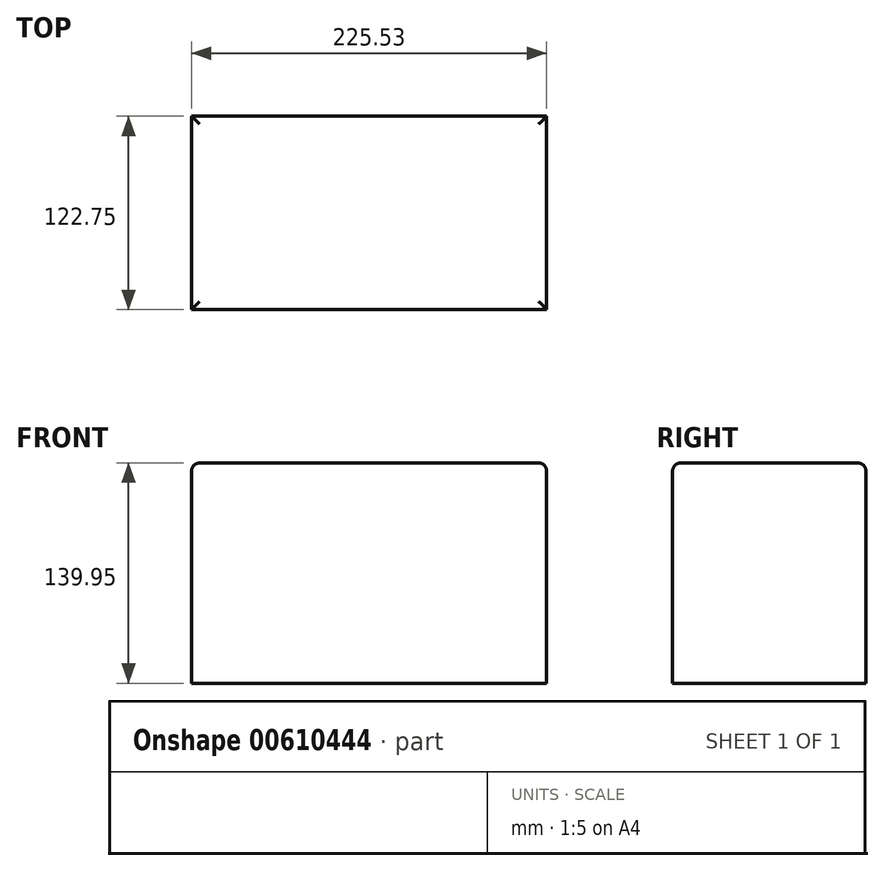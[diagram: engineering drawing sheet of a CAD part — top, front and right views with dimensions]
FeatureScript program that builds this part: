
annotation { "Feature Type Name" : "Feature", "Feature Type Description" : "" }
export const myFeature = defineFeature(function(context is Context, id is Id, definition is map)
    precondition{}
    {
        {
            var Q0;
            Q0=qCreatedBy(makeId("Top.planeOp"),FACE);
            var sketch = newSketch(context, id + "F0", { "sketchPlane" : qUnion([Q0])});
            skLineSegment(sketch, "E0.bottom", {"start": v(-109.76, -69.81) * mm, "end": v(115.77, -69.81) * mm});
            skLineSegment(sketch, "E0.top", {"start": v(-109.76, 52.94) * mm, "end": v(115.77, 52.94) * mm});
            skLineSegment(sketch, "E0.left", {"start": v(-109.76, -69.81) * mm, "end": v(-109.76, 52.94) * mm});
            skLineSegment(sketch, "E0.right", {"start": v(115.77, -69.81) * mm, "end": v(115.77, 52.94) * mm});
            skLineSegment(sketch, "E1.0", {"start": v(-103.4, -69.81) * mm, "end": v(-103.4, 52.94) * mm});
            skSolve(sketch);
        }
        {
            var Q0;
            Q0 = qSketchRegion(id + "F0", true);
            extrude(context, id + "F1", {"entities" : qUnion([Q0]), "depth" : 139.95 * mm, "offsetDistance" : 25.4 * mm});
        }
        {
            var Q0;
            Q0=makeQuery(id+"F1.opExtrude","CAP_EDGE",EDGE,{"disambiguationData":[OSD([sQuery(id+"F0.wireOp",EDGE,"E0.bottom")])],"isStart":false});
            var Q1;
            Q1=makeQuery(id+"F1.opExtrude","CAP_EDGE",EDGE,{"disambiguationData":[OSD([sQuery(id+"F0.wireOp",EDGE,"E0.right")])],"isStart":false});
            var Q2;
            Q2=makeQuery(id+"F1.opExtrude","CAP_EDGE",EDGE,{"disambiguationData":[OSD([sQuery(id+"F0.wireOp",EDGE,"E0.top")])],"isStart":false});
            var Q3;
            Q3=makeQuery(id+"F1.opExtrude","CAP_FACE",FACE,{"disambiguationData":[OSD([sQuery(id+"F0.wireOp",EDGE,"E0.bottom"),sQuery(id+"F0.wireOp",EDGE,"E0.top"),sQuery(id+"F0.wireOp",EDGE,"E0.left"),sQuery(id+"F0.wireOp",EDGE,"E0.right")])],"isStart":false});
            fillet(context, id + "F2", {"entities" : qUnion([Q0, Q1, Q2, Q3]), "radius" : 5.08 * mm, "tangentPropagation" : true, "allowEdgeOverflow" : false});
        }
    });
